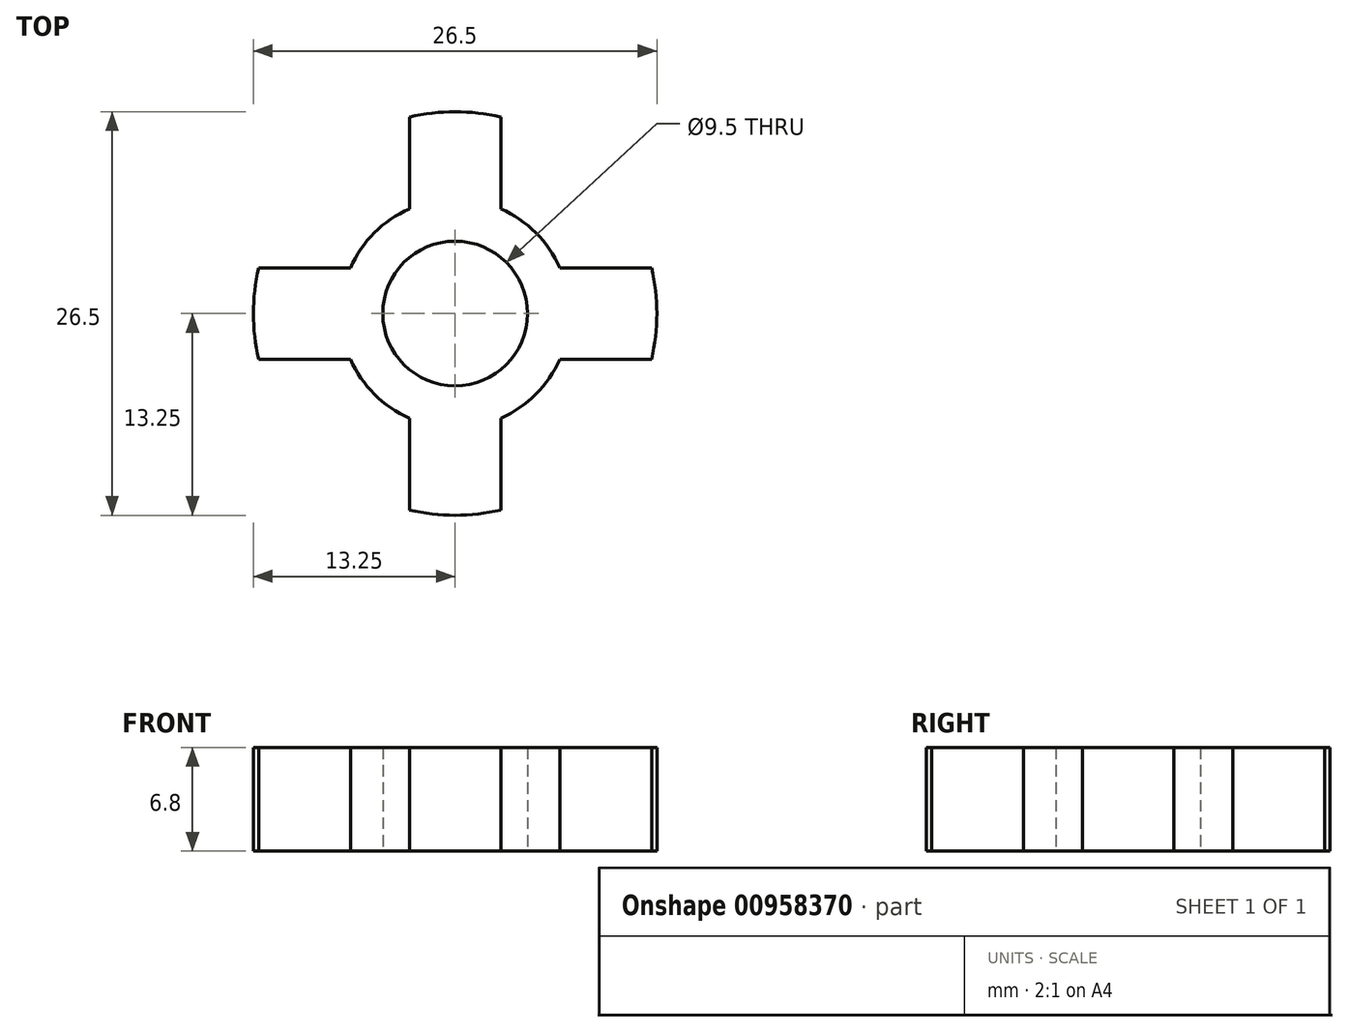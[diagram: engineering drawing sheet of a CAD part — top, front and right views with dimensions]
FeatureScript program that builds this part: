
annotation { "Feature Type Name" : "Feature", "Feature Type Description" : "" }
export const myFeature = defineFeature(function(context is Context, id is Id, definition is map)
    precondition{}
    {
        {
            var Q0;
            Q0=qCreatedBy(makeId("Top.planeOp"),FACE);
            var sketch = newSketch(context, id + "F0", { "sketchPlane" : qUnion([Q0])});
            skCircle(sketch, "E0", {"center": v(0, 0) * mm, "radius": 4.75 * mm});
            skArc(sketch, "E1", {"start": v(-6.87, -3) * mm, "mid": v(-5.3, -5.3) * mm, "end": v(-3, -6.87) * mm});
            skLineSegment(sketch, "E2.left", {"start": v(-3, -12.9) * mm, "end": v(-3, -6.87) * mm});
            skLineSegment(sketch, "E2.right", {"start": v(3, -12.9) * mm, "end": v(3, -6.87) * mm});
            skLineSegment(sketch, "E3.bottom", {"start": v(12.9, 3) * mm, "end": v(6.87, 3) * mm});
            skLineSegment(sketch, "E3.top", {"start": v(12.9, -3) * mm, "end": v(6.87, -3) * mm});
            skLineSegment(sketch, "E4.trimOffspring", {"start": v(-3, 6.87) * mm, "end": v(-3, 12.9) * mm});
            skLineSegment(sketch, "E5.trimOffspring", {"start": v(-6.87, 3) * mm, "end": v(-12.9, 3) * mm});
            skLineSegment(sketch, "E6.trimOffspring", {"start": v(-6.87, -3) * mm, "end": v(-12.9, -3) * mm});
            skLineSegment(sketch, "E7.trimOffspring", {"start": v(3, 6.87) * mm, "end": v(3, 12.9) * mm});
            skPoint(sketch, "E8.orphan", {"position": v(-28.12, -3) * mm});
            skPoint(sketch, "E9.orphan", {"position": v(-28.12, 3) * mm});
            skPoint(sketch, "E10.orphan", {"position": v(-3, 19.51) * mm});
            skPoint(sketch, "E11.orphan", {"position": v(3, 19.51) * mm});
            skPoint(sketch, "E3.left.end.orphan", {"position": v(28.12, -3) * mm});
            skPoint(sketch, "E3.left.start.orphan", {"position": v(28.12, 3) * mm});
            skPoint(sketch, "E12.orphan", {"position": v(3, -19.51) * mm});
            skPoint(sketch, "E13.orphan", {"position": v(-3, -19.51) * mm});
            skArc(sketch, "E14.trimOffspring", {"start": v(3, -6.87) * mm, "mid": v(5.3, -5.3) * mm, "end": v(6.87, -3) * mm});
            skArc(sketch, "E15.trimOffspring", {"start": v(6.87, 3) * mm, "mid": v(5.3, 5.3) * mm, "end": v(3, 6.87) * mm});
            skArc(sketch, "E16.trimOffspring", {"start": v(-3, 6.87) * mm, "mid": v(-5.3, 5.3) * mm, "end": v(-6.87, 3) * mm});
            skArc(sketch, "E17", {"start": v(12.9, -3) * mm, "mid": v(13.25, 0) * mm, "end": v(12.9, 3) * mm});
            skArc(sketch, "E18.trimOffspring", {"start": v(3, 12.9) * mm, "mid": v(0, 13.25) * mm, "end": v(-3, 12.9) * mm});
            skArc(sketch, "E19.trimOffspring", {"start": v(-12.9, 3) * mm, "mid": v(-13.25, 0) * mm, "end": v(-12.9, -3) * mm});
            skArc(sketch, "E20.trimOffspring", {"start": v(-3, -12.9) * mm, "mid": v(0, -13.25) * mm, "end": v(3, -12.9) * mm});
            skSolve(sketch);
        }
        {
            var Q0;
            Q0 = qSketchRegion(id + "F0", true);
            extrude(context, id + "F1", {"entities" : qUnion([Q0]), "depth" : 6.8 * mm, "offsetDistance" : 25 * mm});
        }
    });
